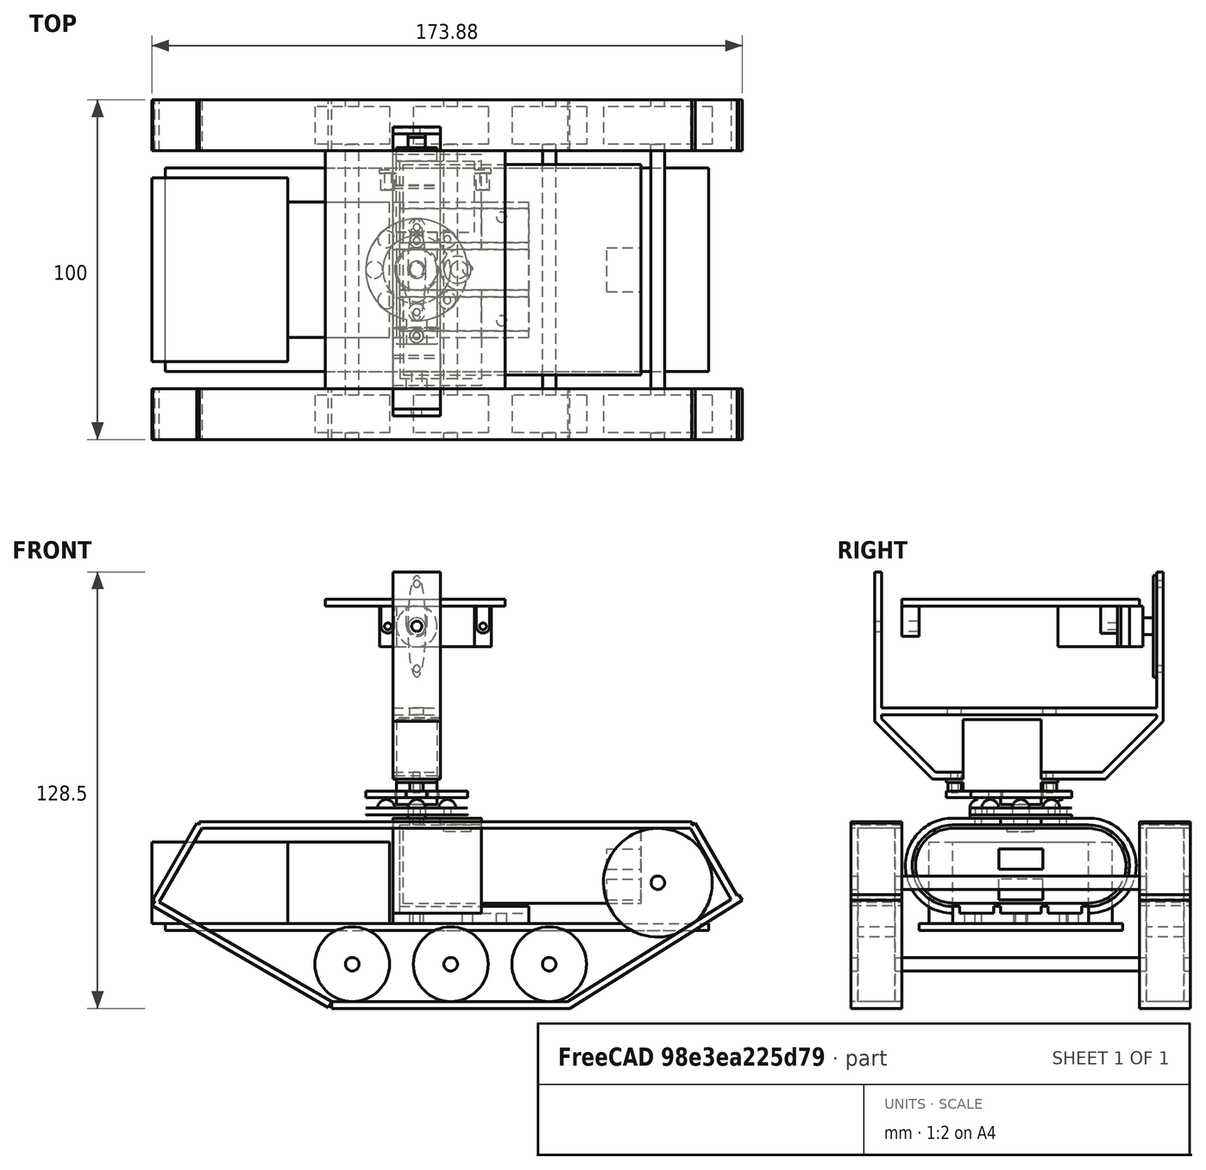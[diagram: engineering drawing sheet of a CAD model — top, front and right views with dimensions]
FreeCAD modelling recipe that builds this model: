
FCSTD DOCUMENT
Label: androidtank_5
License: CC-BY 3.0
LicenseURL: http://creativecommons.org/licenses/by/3.0/
objects: Part::Cylinder×51, Part::Box×36, Part::MultiFuse×24, Part::Sphere×8, Part::Cut×7, App::DocumentObjectGroup×1, Part::FeaturePython×1
note: 127 computed .brp shape members not serialized (recipe doc carries the construction recipe); baked Part::Feature solids carry a one-line shape summary decoded from their .brp

FEATURE [Part::Box] Box  label="MainFrame"
  Height = 2
  Length = 160
  Width = 60
FEATURE [Part::Box] Box001001  label="Moter Unit2"
  Height = 24
  Length = 30
  Placement = pos=(36,10,2) rot=(0,0,1;0rad)
  Width = 40
FEATURE [Part::Cylinder] Cylinder002  label="Wheel1"
  Angle = 360
  Height = 11
  Placement = pos=(20,-7,14) rot=(1,0,0;1.5708rad)
  Radius = 16
FEATURE [Part::Cylinder] Cylinder  label="Shaft"
  Angle = 360
  Height = 100
  Placement = pos=(20,-20,14) rot=(-1,0,0;1.5708rad)
  Radius = 2
FEATURE [Part::Cylinder] Cylinder002001  label="Wheel2"
  Angle = 360
  Height = 11
  Placement = pos=(20,78,14) rot=(1,0,0;1.5708rad)
  Radius = 16
FEATURE [Part::MultiFuse] Fusion001  label="WheelSet2"
  Placement = pos=(125,0,0) rot=(0,0,1;0rad)
  Shapes = -> [Cylinder,Cylinder002,Cylinder002001]
FEATURE [Part::Box] Box001002
  Height = 2
  Length = 145
  Placement = pos=(10,-20,30) rot=(0,0,1;0rad)
  Width = 15
FEATURE [Part::Box] Box001002001
  Height = 2
  Length = 70
  Placement = pos=(49,-20,-23) rot=(0,0,1;0rad)
  Width = 15
FEATURE [Part::Box] Box001002001001
  Height = 2
  Length = 60
  Placement = pos=(119,-20,-23) rot=(0,-1,0;0.558505rad)
  Width = 15
FEATURE [Part::Box] Box001002001002
  Height = 2
  Length = 60
  Placement = pos=(49,-20,-21) rot=(0,1,0;3.66519rad)
  Width = 15
FEATURE [Part::Box] Box001002001003
  Height = 2
  Length = 26
  Placement = pos=(-2,-20,8) rot=(0,-1,0;1.0472rad)
  Width = 15
FEATURE [Part::Box] Box001002001003001
  Height = 2
  Length = 26
  Placement = pos=(169,-20,9) rot=(0,-1,0;2.0944rad)
  Width = 15
FEATURE [Part::MultiFuse] Fusion002001002  label="Caterpiller1"
  Shapes = -> [Box001002,Box001002001,Box001002001002,Box001002001001,Box001002001003,Box001002001003001]
FEATURE [Part::MultiFuse] Fusion002001002001  label="Caterpiller2"
  Placement = pos=(0,85,0) rot=(0,0,1;0rad)
  Shapes = -> [Box001002,Box001002001,Box001002001002,Box001002001001,Box001002001003,Box001002001003001]
FEATURE [Part::Cylinder] Cylinder002001001002  label="Wheel006"
  Angle = 360
  Height = 11
  Placement = pos=(20,78,14) rot=(1,0,0;1.5708rad)
  Radius = 11
FEATURE [Part::Cylinder] Cylinder002001001002001  label="Wheel007"
  Angle = 360
  Height = 11
  Placement = pos=(20,-7,14) rot=(1,0,0;1.5708rad)
  Radius = 11
FEATURE [Part::Cylinder] Cylinder002001002001  label="Shaft002"
  Angle = 360
  Height = 100
  Placement = pos=(20,-20,14) rot=(-1,0,0;1.5708rad)
  Radius = 2
FEATURE [Part::MultiFuse] Fusion002001002002002  label="SWheelSet1"
  Placement = pos=(35,0,-24) rot=(0,0,1;0rad)
  Shapes = -> [Cylinder002001002001,Cylinder002001001002,Cylinder002001001002001]
FEATURE [Part::MultiFuse] Fusion002001002002002001  label="SWheelSet2"
  Placement = pos=(64,0,-24) rot=(0,0,1;0rad)
  Shapes = -> [Cylinder002001002001,Cylinder002001001002,Cylinder002001001002001]
FEATURE [Part::MultiFuse] Fusion002001002002002001001  label="SWheelSet3"
  Placement = pos=(93,0,-24) rot=(0,0,1;0rad)
  Shapes = -> [Cylinder002001002001,Cylinder002001001002,Cylinder002001001002001]
FEATURE [Part::Box] Box001002001003002
  Height = 22
  Length = 70
  Placement = pos=(0,0,-11) rot=(0,0,1;0rad)
  Width = 40
FEATURE [Part::Cylinder] Cylinder002001001002002
  Angle = 360
  Height = 70
  Placement = pos=(0,0,0) rot=(0,1,0;1.5708rad)
  Radius = 11
FEATURE [Part::Cylinder] Cylinder001
  Angle = 360
  Height = 70
  Placement = pos=(0,40,0) rot=(0,1,0;1.5708rad)
  Radius = 11
FEATURE [Part::Cylinder] Cylinder002001001002003  label="PowerButton"
  Angle = 360
  Height = 2
  Placement = pos=(16,20,10) rot=(0,0,1;0rad)
  Radius = 4
FEATURE [Part::Box] Box001002001003003  label="USB1"
  Height = 6
  Length = 15
  Placement = pos=(60,13.5,-1) rot=(0,0,1;0rad)
  Width = 13
FEATURE [Part::Box] Box001001001  label="USB2"
  Height = 6
  Length = 15
  Placement = pos=(60,13.5,-10) rot=(0,0,1;0rad)
  Width = 13
FEATURE [Part::MultiFuse] Fusion002001002002002001002
  Shapes = -> [Cylinder001,Box001002001003002,Cylinder002001001002002]
FEATURE [Part::MultiFuse] Fusion001001
  Shapes = -> [Box001001001,Cylinder002001001002003,Box001002001003003]
FEATURE [Part::Cut] Cut  label="Eneloop"
  Base = -> Fusion002001002002002001002
  Placement = pos=(70,10,19) rot=(0,0,1;0rad)
  Tool = -> Fusion001001
FEATURE [Part::Cylinder] Cylinder001001  label="Cylinder002"
  Angle = 360
  Height = 26
  Placement = pos=(0,50,19) rot=(0,1,0;1.5708rad)
  Radius = 14
FEATURE [Part::Box] Box001002001003002001  label="Box001002001003002001001001001006001001002001003001004"
  Height = 28
  Length = 26
  Placement = pos=(0,10,5) rot=(0,0,1;0rad)
  Width = 40
FEATURE [Part::Cylinder] Cylinder002001001002002001  label="Cylinder003"
  Angle = 360
  Height = 26
  Placement = pos=(0,10,19) rot=(0,1,0;1.5708rad)
  Radius = 14
FEATURE [Part::Box] Box001  label="Moter Unit1"
  Height = 24
  Length = 40
  Placement = pos=(-4,3,2) rot=(0,0,1;0rad)
  Width = 54
FEATURE [App::DocumentObjectGroup] ____________  label="DriveFrame"
  Group = -> [Box,Box001,Box001001,Fusion002001002,Fusion002001002001,Fusion002001002002002,Fusion002001002002002001,Fusion002001002002002001001,Fusion001]
FEATURE [Part::Box] Box001002001003002001001  label="Box003"
  Height = 5
  Length = 40
  Placement = pos=(0,10,2) rot=(0,0,1;0rad)
  Width = 40
FEATURE [Part::Box] Box001002001003002001002  label="Box004"
  Height = 24
  Length = 26
  Placement = pos=(2,10,7) rot=(0,0,1;0rad)
  Width = 40
FEATURE [Part::Cylinder] Cylinder001001001  label="Cylinder004"
  Angle = 360
  Height = 26
  Placement = pos=(2,50,19) rot=(0,1,0;1.5708rad)
  Radius = 12
FEATURE [Part::Cylinder] Cylinder002001001002002001001  label="Cylinder005"
  Angle = 360
  Height = 26
  Placement = pos=(2,10,19) rot=(0,1,0;1.5708rad)
  Radius = 12
FEATURE [Part::Cylinder] Cylinder002001001002003001  label="PowerButton001"
  Angle = 360
  Height = 4
  Placement = pos=(20,30,30) rot=(0,0,1;0rad)
  Radius = 6
FEATURE [Part::Box] Box001002001003002001003  label="Box005"
  Height = 4
  Length = 10
  Placement = pos=(20,24,30) rot=(0,0,1;0rad)
  Width = 12
FEATURE [Part::Box] Box001002001003002001001001  label="Box006"
  Height = 3
  Length = 40
  Placement = pos=(2,12,5) rot=(0,0,1;0rad)
  Width = 10
FEATURE [Part::Box] Box001002001003002001001001001  label="Box007"
  Height = 3
  Length = 40
  Placement = pos=(2,24,5) rot=(0,0,1;0rad)
  Width = 12
FEATURE [Part::Box] Box001002001003002001001001001001  label="Box008"
  Height = 3
  Length = 40
  Placement = pos=(2,38,5) rot=(0,0,1;0rad)
  Width = 10
FEATURE [Part::MultiFuse] Fusion002001002002002001003
  Shapes = -> [Box001002001003002001,Cylinder001001,Cylinder002001001002002001,Box001002001003002001001]
FEATURE [Part::MultiFuse] Fusion002001002002002001004
  Shapes = -> [Box001002001003002001002,Cylinder002001001002002001001,Cylinder001001001,Box001002001003002001001001001001,Box001002001003002001001001001,Box001002001003002001001001,Box001002001003002001003,Cylinder002001001002003001]
FEATURE [Part::Cut] Cut001  label="BatteryFrame"
  Base = -> Fusion002001002002002001003
  Placement = pos=(67,0,0) rot=(0,0,1;0rad)
  Tool = -> Fusion002001002002002001004
FEATURE [Part::Cylinder] Cylinder002001001002002001002001  label="Cylinder007"
  Angle = 360
  Height = 40
  Placement = pos=(74,17.5,0) rot=(0,0,1;0rad)
  Radius = 1
FEATURE [Part::Cylinder] Cylinder002001001002002001002  label="Cylinder006"
  Angle = 360
  Height = 40
  Placement = pos=(74,42.5,0) rot=(0,0,1;0rad)
  Radius = 1
FEATURE [Part::Cylinder] Cylinder002001001002002001002001001  label="Cylinder008"
  Angle = 360
  Height = 40
  Placement = pos=(89,30,0) rot=(0,0,1;0rad)
  Radius = 1.5
FEATURE [Part::Cylinder] Cylinder002001001002002001002001002  label="Cylinder009"
  Angle = 360
  Height = 40
  Placement = pos=(99,45.5,0) rot=(0,0,1;0rad)
  Radius = 1.5
FEATURE [Part::Cylinder] Cylinder002001001002002001002001003  label="Cylinder0010"
  Angle = 360
  Height = 40
  Placement = pos=(99,15,0) rot=(0,0,1;0rad)
  Radius = 1.5
FEATURE [Part::Box] Box001002001003002001001001001006  label="Box009"
  Height = 2
  Length = 53
  Placement = pos=(47,-5,100) rot=(0,0,1;0rad)
  Width = 70
FEATURE [Part::Box] Box001002001003002001001001001006001  label="Box010"
  Height = 44
  Length = 14
  Placement = pos=(67,70,66) rot=(0,0,1;0rad)
  Width = 2
FEATURE [Part::Box] Box001002001003002001001001001006001001  label="Box011"
  Height = 2
  Length = 13
  Placement = pos=(67.5,12.5,48) rot=(0,0,1;0rad)
  Width = 23.5
FEATURE [Part::Box] Box001002001003002001001001001006001001001  label="Box012"
  Height = 44
  Length = 14
  Placement = pos=(67,-13,66) rot=(0,0,1;0rad)
  Width = 2
FEATURE [Part::Cylinder] Cylinder002001001002002001002001008  label="Hole1"
  Angle = 360
  Height = 20
  Placement = pos=(74,-20,94) rot=(-1,0,0;1.5708rad)
  Radius = 1.5
FEATURE [Part::Cylinder] Cylinder002001001002002001002001008001  label="Hole2"
  Angle = 360
  Height = 20
  Placement = pos=(74,60,106.5) rot=(-1,0,0;1.5708rad)
  Radius = 1
FEATURE [Part::Cylinder] Cylinder002001001002002001002001008001001  label="Hole4"
  Angle = 360
  Height = 20
  Placement = pos=(74,38.5,41) rot=(0,0,1;0rad)
  Radius = 1
FEATURE [Part::Cylinder] Cylinder002001001002002001002001008001001001  label="Hole3"
  Angle = 360
  Height = 20
  Placement = pos=(74,60,81.5) rot=(-1,0,0;1.5708rad)
  Radius = 1
FEATURE [Part::Cylinder] Cylinder002001001002002001002001008001001002  label="Hole5"
  Angle = 360
  Height = 20
  Placement = pos=(74,10.5,41) rot=(0,0,1;0rad)
  Radius = 1
FEATURE [Part::Box] Box001002001003002001001001001006001001001001  label="Box013"
  Height = 24
  Length = 14
  Placement = pos=(67,4,49) rot=(1,0,0;0.785397rad)
  Width = 2
FEATURE [Part::Box] Box001002001003002001001001001006001001001001001  label="Box014"
  Height = 24
  Length = 14
  Placement = pos=(67,53.41,50.41) rot=(-1,0,0;0.785397rad)
  Width = 2
FEATURE [Part::Box] Box001002001003002001001001001006001001002001  label="Box016"
  Height = 2
  Length = 14
  Placement = pos=(67,4,49) rot=(0,0,1;0rad)
  Width = 9
FEATURE [Part::Box] Box001002001003002001001001001006001001002001001  label="Box017"
  Height = 2
  Length = 14
  Placement = pos=(67,36,49) rot=(0,0,1;0rad)
  Width = 19
FEATURE [Part::Box] Box001002001003002001001001001006001001002001002  label="Box015"
  Height = 2
  Length = 14
  Placement = pos=(67,-13,68) rot=(0,0,1;0rad)
  Width = 85
FEATURE [Part::MultiFuse] Fusion002001002002002001009
  Shapes = -> [Box001002001003002001001001001006001,Box001002001003002001001001001006001001001001,Box001002001003002001001001001006001001001,Box001002001003002001001001001006001001001001001,Box001002001003002001001001001006001001002001,Box001002001003002001001001001006001001002001002,Box001002001003002001001001001006001001002001001]
FEATURE [Part::Cylinder] Cylinder002001001002002001002001008001001002001  label="Hole006"
  Angle = 360
  Height = 20
  Placement = pos=(74,10.5,60) rot=(0,0,1;0rad)
  Radius = 2
FEATURE [Part::Cylinder] Cylinder002001001002002001002001008001001002002  label="Hole007"
  Angle = 360
  Height = 20
  Placement = pos=(74,38.5,60) rot=(0,0,1;0rad)
  Radius = 2
FEATURE [Part::MultiFuse] Fusion002001002002002001010
  Shapes = -> [Cylinder002001001002002001002001008001,Box001002001003002001001001001006001001,Cylinder002001001002002001002001008001001,Cylinder002001001002002001002001008,Cylinder002001001002002001002001008001001001,Cylinder002001001002002001002001008001001002,Cylinder002001001002002001002001008001001002002,Cylinder002001001002002001002001008001001002001]
FEATURE [Part::Cut] Cut003  label="HeadFrame"
  Base = -> Fusion002001002002002001009
  Placement = pos=(0,0,-4.5) rot=(0,0,1;0rad)
  Tool = -> Fusion002001002002002001010
FEATURE [Part::Cylinder] Cylinder002001001002002001002001008001001002003  label="Cylinder025"
  Angle = 360
  Height = 5
  Placement = pos=(74,0,94) rot=(1,0,0;1.5708rad)
  Radius = 3
FEATURE [Part::Box] Box001002001003002001001001001006001001002001003  label="Box020"
  Height = 6
  Length = 6
  Placement = pos=(71,-5,94) rot=(0,0,1;0rad)
  Width = 5
FEATURE [Part::Cylinder] Cylinder002001001002002001002001008001001002003001  label="Cylinder026"
  Angle = 360
  Height = 7
  Placement = pos=(74,1,94) rot=(1,0,0;1.5708rad)
  Radius = 1.5
FEATURE [Part::Box] Box001002001003002001001001001006001001002001003001001  label="Box022"
  Height = 6
  Length = 4
  Placement = pos=(91.5,53.5,94) rot=(0,0,1;0rad)
  Width = 5
FEATURE [Part::Cylinder] Cylinder002001001002002001002001008001001002003002  label="Cylinder027"
  Angle = 360
  Height = 5
  Placement = pos=(65.5,58.5,94) rot=(1,0,0;1.5708rad)
  Radius = 2
FEATURE [Part::Cylinder] Cylinder002001001002002001002001008001001002003002001  label="Cylinder028"
  Angle = 360
  Height = 5
  Placement = pos=(93.5,58.5,94) rot=(1,0,0;1.5708rad)
  Radius = 2
FEATURE [Part::Box] Box001002001003002001001001001006001001002001003001  label="Box021"
  Height = 6
  Length = 4
  Placement = pos=(63.5,53.5,94) rot=(0,0,1;0rad)
  Width = 5
FEATURE [Part::Cylinder] Cylinder002001001002002001002001008001001002003002002  label="Cylinder029"
  Angle = 360
  Height = 6
  Placement = pos=(65.5,59,94) rot=(1,0,0;1.5708rad)
  Radius = 1
FEATURE [Part::Cylinder] Cylinder002001001002002001002001008001001002003002001001  label="Cylinder030"
  Angle = 360
  Height = 6
  Placement = pos=(93.5,59,94) rot=(1,0,0;1.5708rad)
  Radius = 1
FEATURE [Part::MultiFuse] Fusion002001002002002001011
  Shapes = -> [Box001002001003002001001001001006,Box001002001003002001001001001006001001002001003001001,Cylinder002001001002002001002001008001001002003002001,Box001002001003002001001001001006001001002001003,Cylinder002001001002002001002001008001001002003,Box001002001003002001001001001006001001002001003001,Cylinder002001001002002001002001008001001002003002]
FEATURE [Part::MultiFuse] Fusion002001002002002001012
  Shapes = -> [Cylinder002001001002002001002001008001001002003001,Cylinder002001001002002001002001008001001002003002002,Cylinder002001001002002001002001008001001002003002001001]
FEATURE [Part::Cut] Cut002003  label="HeadMount"
  Base = -> Fusion002001002002002001011
  Placement = pos=(0,0,-4.5) rot=(0,0,1;0rad)
  Tool = -> Fusion002001002002002001012
FEATURE [Part::Cylinder] Cylinder002001001002002001002001001001  label="Cylinder040"
  Angle = 360
  Height = 40
  Placement = pos=(74,30,0) rot=(0,0,1;0rad)
  Radius = 2
FEATURE [Part::MultiFuse] Fusion002001002002002001013  label="BatteryFrameHoles"
  Shapes = -> [Cylinder002001001002002001002001,Cylinder002001001002002001002,Cylinder002001001002002001002001001,Cylinder002001001002002001002001002,Cylinder002001001002002001002001003,Cylinder002001001002002001002001001001]
FEATURE [Part::Cut] Cut002004  label="BatteryFrame2"
  Base = -> Cut001
  Tool = -> Fusion002001002002002001013
FEATURE [Part::Box] Box001002001003002001001001001006001001002001003001002  label="ServoBody"
  Height = 21
  Length = 23
  Width = 12
FEATURE [Part::Cylinder] Cylinder002001001002002001002001008001001002003002001002  label="ServoBody2"
  Angle = 360
  Height = 4
  Placement = pos=(6,6,21) rot=(0,0,1;0rad)
  Radius = 6
FEATURE [Part::Box] Box001002001003002001001001001006001001002001003001003  label="ServoBody3"
  Height = 1
  Length = 33
  Placement = pos=(-5,0,17.5) rot=(0,0,1;0rad)
  Width = 12
FEATURE [Part::Cylinder] Cylinder001001002  label="ServoAxis"
  Angle = 360
  Height = 4
  Placement = pos=(6,6,24) rot=(0,0,1;0rad)
  Radius = 2.5
FEATURE [Part::MultiFuse] Fusion005  label="ServoArmL"
  Shapes = -> [Cylinder001001002,Box001002001003002001001001001006001001002001003001003,Box001002001003002001001001001006001001002001003001002,Cylinder002001001002002001002001008001001002003002001002]
FEATURE [Part::MultiFuse] Fusion006  label="ServoYaw"
  Placement = pos=(80,36,62) rot=(0.707107,-0.707107,0;3.14159rad)
  Shapes = -> [Fusion005]
FEATURE [Part::Cylinder] Cylinder003001001003002  label="Cylinder002001001002002001002001008001001002003002001004"
  Angle = 360
  Height = 2
  Placement = pos=(6,6,26) rot=(0,0,1;0rad)
  Radius = 15
FEATURE [Part::Cylinder] Cylinder003001001004  label="Cylinder002001001002002001002001008001001002003002001005"
  Angle = 360
  Height = 3
  Placement = pos=(-2.5,6,18.4) rot=(0,0,1;0rad)
  Radius = 2
FEATURE [Part::Cylinder] Cylinder003001001005  label="Cylinder011"
  Angle = 360
  Height = 2
  Placement = pos=(6,6,21) rot=(0,0,1;0rad)
  Radius = 15
FEATURE [Part::Cylinder] Cylinder003001001004001  label="Cylinder010"
  Angle = 360
  Height = 3
  Placement = pos=(25.5,6,18.4) rot=(0,0,1;0rad)
  Radius = 2
FEATURE [Part::Cylinder] Cylinder003001001005001  label="Cylinder012"
  Angle = 360
  Height = 2
  Placement = pos=(6,6,21) rot=(0,0,1;0rad)
  Radius = 6.5
FEATURE [Part::Cylinder] Cylinder003001001005001001  label="Cylinder013"
  Angle = 360
  Height = 2
  Placement = pos=(12,6,21) rot=(0,0,1;0rad)
  Radius = 3.5
FEATURE [Part::Box] Box002
  Height = 2
  Length = 10
  Placement = pos=(18,3,21) rot=(0,0,1;0rad)
  Width = 6
FEATURE [Part::Cylinder] Cylinder003001001004002  label="Cylinder014"
  Angle = 360
  Height = 5
  Placement = pos=(-2.5,6,16.4) rot=(0,0,1;0rad)
  Radius = 1
FEATURE [Part::Cylinder] Cylinder003001001004001001  label="Cylinder015"
  Angle = 360
  Height = 5
  Placement = pos=(25.5,6,16.4) rot=(0,0,1;0rad)
  Radius = 1
FEATURE [Part::MultiFuse] Fusion008
  Shapes = -> [Cylinder003001001005,Box002,Cylinder003001001004,Cylinder003001001004001]
FEATURE [Part::MultiFuse] Fusion009
  Shapes = -> [Cylinder003001001005001,Cylinder003001001005001001,Cylinder003001001004002,Cylinder003001001004001001]
FEATURE [Part::Cut] Cut002  label="Guide1"
  Base = -> Fusion008
  Placement = pos=(80,36,62) rot=(-0.705662,0.708549,0;3.14159rad)
  Tool = -> Fusion009
FEATURE [Part::Sphere] Sphere001001001001001001002
  Angle1 = -90
  Angle2 = 0
  Angle3 = 360
  Placement = pos=(-3,-3,26) rot=(0,0,1;0rad)
  Radius = 2.5
FEATURE [Part::Sphere] Sphere001001001001001001003
  Angle1 = -90
  Angle2 = 0
  Angle3 = 360
  Placement = pos=(15,-3,26) rot=(0,0,1;0rad)
  Radius = 2.5
FEATURE [Part::Sphere] Sphere001001001001001001004  label="Sphere001001001001001001001002"
  Angle1 = -90
  Angle2 = 0
  Angle3 = 360
  Placement = pos=(15,15,26) rot=(0,0,1;0rad)
  Radius = 2.5
FEATURE [Part::Sphere] Sphere001001001001001001005  label="Sphere001001001001001001001003"
  Angle1 = -90
  Angle2 = 0
  Angle3 = 360
  Placement = pos=(-3,15,26) rot=(0,0,1;0rad)
  Radius = 2.5
FEATURE [Part::Cylinder] Cylinder003001001005001004001  label="Cylinder002001001002002001002001008001001002003002001006"
  Angle = 360
  Height = 4
  Placement = pos=(-6.5,6,26) rot=(0,0,1;0rad)
  Radius = 1
FEATURE [Part::Cylinder] Cylinder003001001001003001  label="Cylinder002001001002002001002001008001001002003002001007"
  Angle = 360
  Height = 4
  Placement = pos=(18.5,6,26) rot=(0,0,1;0rad)
  Radius = 1
FEATURE [Part::Cylinder] Cylinder003001001005001003001001  label="Cylinder002001001002002001002001008001001002003002001008"
  Angle = 360
  Height = 5
  Placement = pos=(-3,-3,26) rot=(0,0,1;0rad)
  Radius = 1
FEATURE [Part::Cylinder] Cylinder003001001001002001001  label="Cylinder002001001002002001002001008001001002003002001009"
  Angle = 360
  Height = 5
  Placement = pos=(15,-3,26) rot=(0,0,1;0rad)
  Radius = 1
FEATURE [Part::Sphere] Sphere001001001001001001006  label="Sphere001001001001001001001004"
  Angle1 = -90
  Angle2 = 0
  Angle3 = 360
  Placement = pos=(-6.5,6,26) rot=(0,0,1;0rad)
  Radius = 2.5
FEATURE [Part::Sphere] Sphere001001001001001001007  label="Sphere001001001001001001001005"
  Angle1 = -90
  Angle2 = 0
  Angle3 = 360
  Placement = pos=(18.5,6,26) rot=(0,0,1;0rad)
  Radius = 2.5
FEATURE [Part::Sphere] Sphere001001001001001001008  label="Sphere001001001001001001001006"
  Angle1 = -90
  Angle2 = 0
  Angle3 = 360
  Placement = pos=(6,-6.5,26) rot=(0,0,1;0rad)
  Radius = 2.5
FEATURE [Part::Sphere] Sphere001001001001001001001001  label="Sphere001001001001001001001007"
  Angle1 = -90
  Angle2 = 0
  Angle3 = 360
  Placement = pos=(6,18.5,26) rot=(0,0,1;0rad)
  Radius = 2.5
FEATURE [Part::Cylinder] Cylinder003001001003001001  label="Cylinder002001001002002001002001008001001002003002001010"
  Angle = 360
  Height = 2
  Placement = pos=(6,6,26) rot=(0,0,1;0rad)
  Radius = 10
FEATURE [Part::MultiFuse] Fusion013001
  Shapes = -> [Cylinder003001001003001001,Cylinder003001001005001003001001,Cylinder003001001001002001001,Cylinder003001001005001004001,Cylinder003001001001003001]
FEATURE [Part::MultiFuse] Fusion014
  Shapes = -> [Sphere001001001001001001002,Cylinder003001001003002,Sphere001001001001001001005,Sphere001001001001001001008,Sphere001001001001001001006,Sphere001001001001001001003,Sphere001001001001001001004,Sphere001001001001001001001001,Sphere001001001001001001007]
FEATURE [Part::Cut] Cut002005  label="Guide2"
  Base = -> Fusion014
  Placement = pos=(80,36,62) rot=(0.707107,-0.707107,0;3.14159rad)
  Tool = -> Fusion013001
FEATURE [Part::Box] Box001002001003002001001001001006001001002001003001004  label="ServoBody004"
  Height = 21
  Length = 23
  Width = 12
FEATURE [Part::Cylinder] Cylinder002001001002002001002001008001001002003002001003  label="ServoBody005"
  Angle = 360
  Height = 4
  Placement = pos=(6,6,21) rot=(0,0,1;0rad)
  Radius = 6
FEATURE [Part::Box] Box001002001003002001001001001006001001002001003001005  label="ServoBody006"
  Height = 1
  Length = 33
  Placement = pos=(-5,0,17.5) rot=(0,0,1;0rad)
  Width = 12
FEATURE [Part::Cylinder] Cylinder001001003  label="ServoAxis001"
  Angle = 360
  Height = 4
  Placement = pos=(6,6,24) rot=(0,0,1;0rad)
  Radius = 2.5
FEATURE [Part::MultiFuse] Fusion005001  label="ServoArmL001"
  Shapes = -> [Cylinder001001003,Box001002001003002001001001001006001001002001003001005,Box001002001003002001001001001006001001002001003001004,Cylinder002001001002002001002001008001001002003002001003]
FEATURE [Part::Cylinder] Cylinder002001001002002001002001008001001002003002001004  label="Cylinder002001001002002001002001008001001002003002001011"
  Angle = 360
  Height = 2
  Radius = 2.5
FEATURE [Part::FeaturePython] Scale  # Draft clone (typed FeaturePython)
  Objects = -> [Cylinder002001001002002001002001008001001002003002001004]
  Placement = pos=(0,0,1) rot=(0,0,1;0rad)
  Scale = (6,1,0.5)
FEATURE [Part::MultiFuse] Fusion  label="Arm"
  Placement = pos=(6,6,27) rot=(0,0,1;1.5708rad)
  Shapes = -> [Cylinder002001001002002001002001008001001002003002001004,Scale]
FEATURE [Part::MultiFuse] Fusion006001  label="ServoPitch"
  Placement = pos=(68,41,95.5) rot=(-1,0,0;1.5708rad)
  Shapes = -> [Fusion005001,Fusion]
